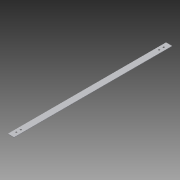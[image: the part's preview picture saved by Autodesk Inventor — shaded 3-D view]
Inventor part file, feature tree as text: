
AUTODESK INVENTOR PART (.ipt)
format: ipt  version: 2013 (Build 170138000, 138)  size: 81,920 bytes
history: native  units: in
note: dims shown in document units (in); Inventor stores cm internally (conversion verified against a paired STEP export)
features: extrude x1, sketch x1
ambient origin geometry x8: Origin, YZ Plane, XZ Plane, XY Plane, X Axis, Y Axis, Z Axis, Center Point
bodies: Solid1 (feature_tree)
feature tree (2):
  extrude  "Extrusion1"  Depth=1.0in
  sketch  "Sketch1"  dims[d0=26.0in d1=1.0in d2=0.0625in d3=0.0in d4=0.266in d5=0.875in d6=0.75in d7=0.875in d8=0.75in]
